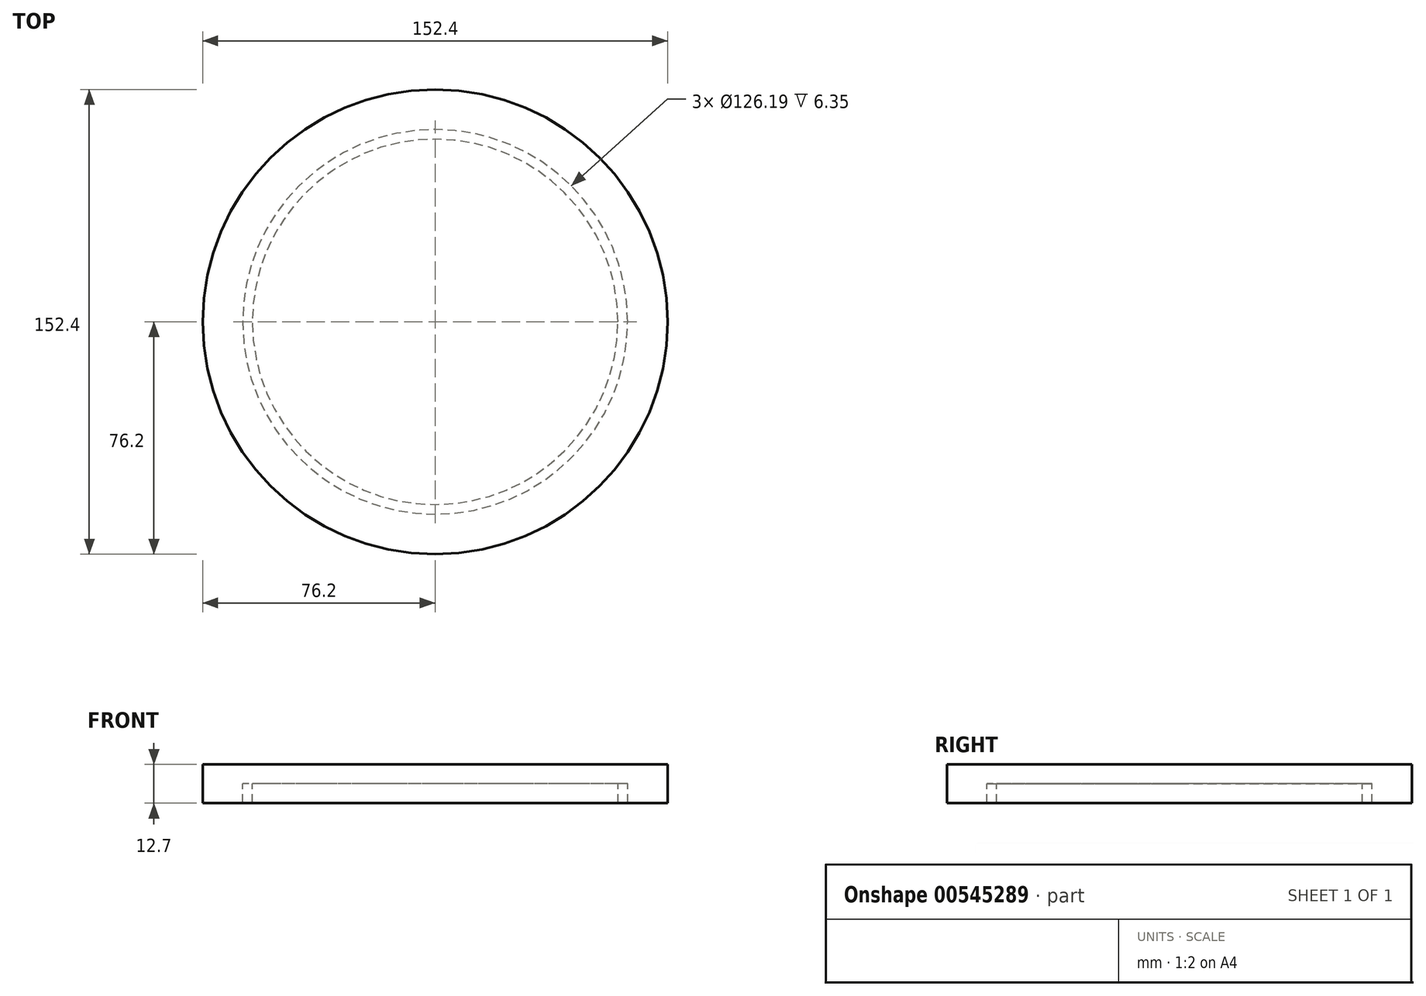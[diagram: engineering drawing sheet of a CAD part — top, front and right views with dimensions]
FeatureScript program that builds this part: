
annotation { "Feature Type Name" : "Feature", "Feature Type Description" : "" }
export const myFeature = defineFeature(function(context is Context, id is Id, definition is map)
    precondition{}
    {
        {
            var Q0;
            Q0=qCreatedBy(makeId("Front.planeOp"),FACE);
            var sketch = newSketch(context, id + "F0", { "sketchPlane" : qUnion([Q0])});
            skLineSegment(sketch, "E0", {"start": v(0, 0) * mm, "end": v(76.2, 0) * mm});
            skLineSegment(sketch, "E1", {"start": v(0, 0) * mm, "end": v(0, -12.7) * mm});
            skLineSegment(sketch, "E2", {"start": v(0, -12.7) * mm, "end": v(59.92, -12.7) * mm});
            skLineSegment(sketch, "E3", {"start": v(59.92, -6.35) * mm, "end": v(59.92, -12.7) * mm});
            skLineSegment(sketch, "E4", {"start": v(59.92, -6.35) * mm, "end": v(63.1, -6.35) * mm});
            skLineSegment(sketch, "E5", {"start": v(63.1, -6.35) * mm, "end": v(63.1, -12.7) * mm});
            skLineSegment(sketch, "E6", {"start": v(63.1, -12.7) * mm, "end": v(76.2, -12.7) * mm});
            skLineSegment(sketch, "E7", {"start": v(76.2, 0) * mm, "end": v(76.2, -12.7) * mm});
            skSolve(sketch);
        }
        {
            var Q0;
            Q0=makeQuery(id+"F0.imprint","IMPRINT",FACE,{"disambiguationData":[TD([[makeQuery(id+"F0.imprint","IMPRINT",EDGE,{"derivedFrom":sQuery(id+"F0.wireOp",EDGE,"E0")}),-1.0]])]});
            var Q1;
            Q1=sQuery(id+"F0.wireOp",EDGE,"E1");
            revolve(context, id + "F1", {"entities" : qUnion([Q0]), "axis" : qUnion([Q1]), "revolveType" : RevolveType.FULL});
        }
    });
